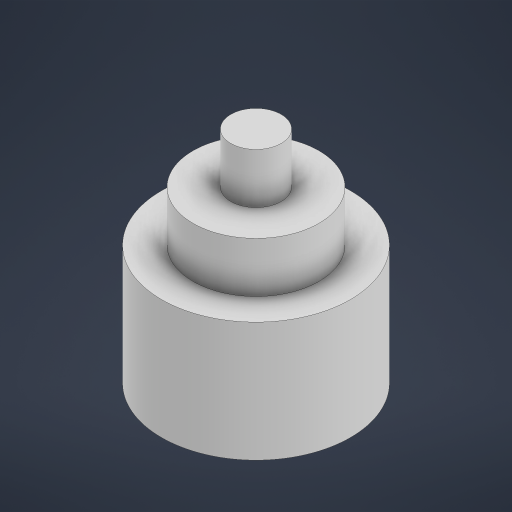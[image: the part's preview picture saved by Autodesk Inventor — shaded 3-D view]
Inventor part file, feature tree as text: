
AUTODESK INVENTOR PART (.ipt)
format: ipt  version: 2023 (Build 270158030, 158C)  size: 203,776 bytes
history: native  units: in
note: dims shown in document units (in); Inventor stores cm internally (conversion verified against a paired STEP export)
features: extrude x4, sketch x3
ambient origin geometry x8: Origin, YZ Plane, XZ Plane, XY Plane, X Axis, Y Axis, Z Axis, Center Point
bodies: Solid1 (feature_tree)
feature tree (7):
  extrude  "Extrusion1"  Depth=1.378in TaperAngle=0.0deg
  sketch  "Sketch3"  dims[d3=0.315in d4=0.7874in]
  extrude  "Extrusion2"  Depth=0.315in
  extrude  "Extrusion3"  Depth=0.315in TaperAngle=0.0deg
  extrude  "Extrusion4"  Depth=0.1575in
  sketch  "Sketch2"  dims[d0=1.1811in d1=1.378in d2=0.0in]
  sketch  "Sketch4"  dims[d5=0.6299in d6=0.0in d7=0.315in d8=0.0in d9=0.3543in d10=0.1575in d11=0.0in]
